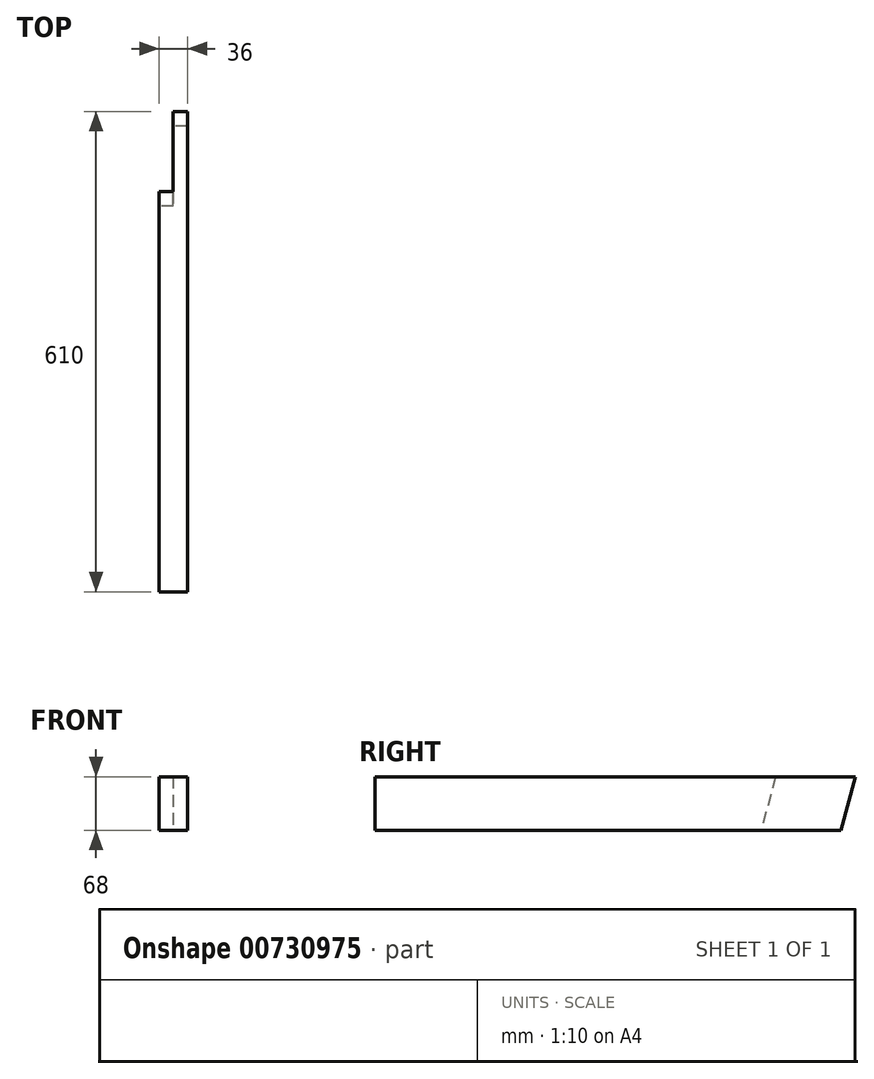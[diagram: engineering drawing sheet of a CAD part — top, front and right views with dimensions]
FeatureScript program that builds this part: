
annotation { "Feature Type Name" : "Feature", "Feature Type Description" : "" }
export const myFeature = defineFeature(function(context is Context, id is Id, definition is map)
    precondition{}
    {
        {
            var Q0;
            Q0=qCreatedBy(makeId("Front.planeOp"),FACE);
            var sketch = newSketch(context, id + "F0", { "sketchPlane" : qUnion([Q0])});
            skLineSegment(sketch, "E0.bottom", {"start": v(18, -34) * mm, "end": v(-18, -34) * mm});
            skLineSegment(sketch, "E0.top", {"start": v(18, 34) * mm, "end": v(-18, 34) * mm});
            skLineSegment(sketch, "E0.left", {"start": v(18, -34) * mm, "end": v(18, 34) * mm});
            skLineSegment(sketch, "E0.right", {"start": v(-18, -34) * mm, "end": v(-18, 34) * mm});
            skPoint(sketch, "E0.middle", {"position": v(0, 0) * mm});
            skSolve(sketch);
        }
        {
            var Q0;
            Q0=makeQuery(id+"F0.imprint","IMPRINT",FACE,{"disambiguationData":[TD([[makeQuery(id+"F0.imprint","IMPRINT",EDGE,{"derivedFrom":sQuery(id+"F0.wireOp",EDGE,"E0.bottom")}),-1.0]])]});
            extrude(context, id + "F1", {"entities" : qUnion([Q0]), "depth" : 610 * mm, "offsetDistance" : 25 * mm});
        }
        {
            var Q0;
            Q0=makeQuery(id+"F1.opExtrude","SWEPT_FACE",FACE,{"disambiguationData":[OSD([sQuery(id+"F0.wireOp",EDGE,"E0.right")])]});
            var sketch = newSketch(context, id + "F2", { "sketchPlane" : qUnion([Q0])});
            skLineSegment(sketch, "E1", {"start": v(0, 34) * mm, "end": v(18.22, -34) * mm});
            skLineSegment(sketch, "E2", {"start": v(18.22, -34) * mm, "end": v(0, -34) * mm});
            skLineSegment(sketch, "E3", {"start": v(0, -34) * mm, "end": v(0, 34) * mm});
            skSolve(sketch);
        }
        {
            var Q0;
            Q0=makeQuery(id+"F2.imprint","IMPRINT",FACE,{"disambiguationData":[TD([[makeQuery(id+"F2.imprint","IMPRINT",EDGE,{"derivedFrom":sQuery(id+"F2.wireOp",EDGE,"E1")}),-1.0]])]});
            extrude(context, id + "F3", {"entities" : qUnion([Q0]), "operationType" : NewBodyOperationType.REMOVE, "endBound" : BoundingType.UP_TO_NEXT, "oppositeDirection" : true, "depth" : 25 * mm, "offsetDistance" : 25 * mm});
        }
        {
            var Q0;
            Q0=makeQuery(id+"F1.opExtrude","SWEPT_FACE",FACE,{"disambiguationData":[OSD([sQuery(id+"F0.wireOp",EDGE,"E0.right")])]});
            var sketch = newSketch(context, id + "F4", { "sketchPlane" : qUnion([Q0])});
            skLineSegment(sketch, "E4", {"start": v(0, 34) * mm, "end": v(101.5, 34) * mm});
            skLineSegment(sketch, "E5", {"start": v(101.5, 34) * mm, "end": v(119.72, -34) * mm});
            skLineSegment(sketch, "E6", {"start": v(119.72, -34) * mm, "end": v(18.22, -34) * mm});
            skLineSegment(sketch, "E7", {"start": v(18.22, -34) * mm, "end": v(0, 34) * mm});
            skSolve(sketch);
        }
        {
            var Q0;
            Q0=makeQuery(id+"F4.imprint","IMPRINT",FACE,{"disambiguationData":[TD([[makeQuery(id+"F4.imprint","IMPRINT",EDGE,{"derivedFrom":sQuery(id+"F4.wireOp",EDGE,"E4")}),1.0]])]});
            extrude(context, id + "F5", {"entities" : qUnion([Q0]), "operationType" : NewBodyOperationType.REMOVE, "oppositeDirection" : true, "depth" : 18 * mm, "offsetDistance" : 25 * mm});
        }
    });
